# Revit family: Faucet-Deck_Mount-Bath-KOHLER-Forte-K-T10278_1
name_source: partatom
category: Plumbing Fixtures
revit_build: Autodesk Revit 2015 (Build: 20140606_1530(x64)
units: mm (PartAtom-declared; Revit-internal decimal feet)

## types (6) — shared parameters
ADA Compliant = Yes
Assembly Code = D2010
CW Connection = Yes
Cold Water Inlet = Cold Water Inlet
Date Modified = 02/26/2019
Default Elevation = 36"
Drain Included = No
Flow Rate = 0 GPM
HW Connection = Yes
Height = 6 3/4"
Hot Water Inlet = Hot Water Inlet
Length = 7"
Manufacturer = KOHLER Co.
MasterFormat 1995 = 15410
MasterFormat 2004 = 22.41.39
Material = Brass construction
Pressure = 0.00 psi
Product Documentation Link = https://www.us.kohler.com
Product Name = Forte
Product Page URL = http://www.us.kohler.com
Spout Reach = 7"
URL = https://www.us.kohler.com
Vent Connection = No
Waste Connection = No
Waste Water Outlet = Waste Water Outlet
WaterSense Certified = No

## per-type parameters (varying)
| type | Description | Finish | Handle Clearance | Handle Height | Model | Sculpted-4 | Traditional-4A | Type |
| Sculpted, CP-Polished Chrome | Sculpted deck-mount bath faucet trim for high-flow valve, valve not included | Kohler-Metal-CP-Polished_Chrome | 2 7/8" | 4 5/8" | K-T10278-4-CP | Yes | No | 1 |
| Sculpted, G-Brushed Chrome | Sculpted deck-mount bath faucet trim for high-flow valve, valve not included | Kohler-Metal-G-Brushed_Chrome | 2 7/8" | 4 5/8" | K-T10278-4-G | Yes | No | 2 |
| Sculpted, BN-Vibrant Brushed Nickel | Sculpted deck-mount bath faucet trim for high-flow valve, valve not included | Kohler-Metal-BN-Vibrant_Brushed_Nickel | 2 7/8" | 4 5/8" | K-T10278-4-BN | Yes | No | 3 |
| Traditional, CP-Polished Chrome | Traditional deck-mount bath faucet trim for high-flow valve, valve not included | Kohler-Metal-CP-Polished_Chrome | 3" | 4 11/16" | K-T10278-4A-CP | No | Yes | 4 |
| Traditional, G-Brushed Chrome | Traditional deck-mount bath faucet trim for high-flow valve, valve not included | Kohler-Metal-G-Brushed_Chrome | 3" | 4 11/16" | K-T10278-4A-G | No | Yes | 5 |
| Traditional, BN-Vibrant Brushed Nickel | Traditional deck-mount bath faucet trim for high-flow valve, valve not included | Kohler-Metal-BN-Vibrant_Brushed_Nickel | 3" | 4 11/16" | K-T10278-4A-BN | No | Yes | 6 |

## geometry (parser evidence)
native form markers: Sweep x8
no freeform markers — native parametric forms only
